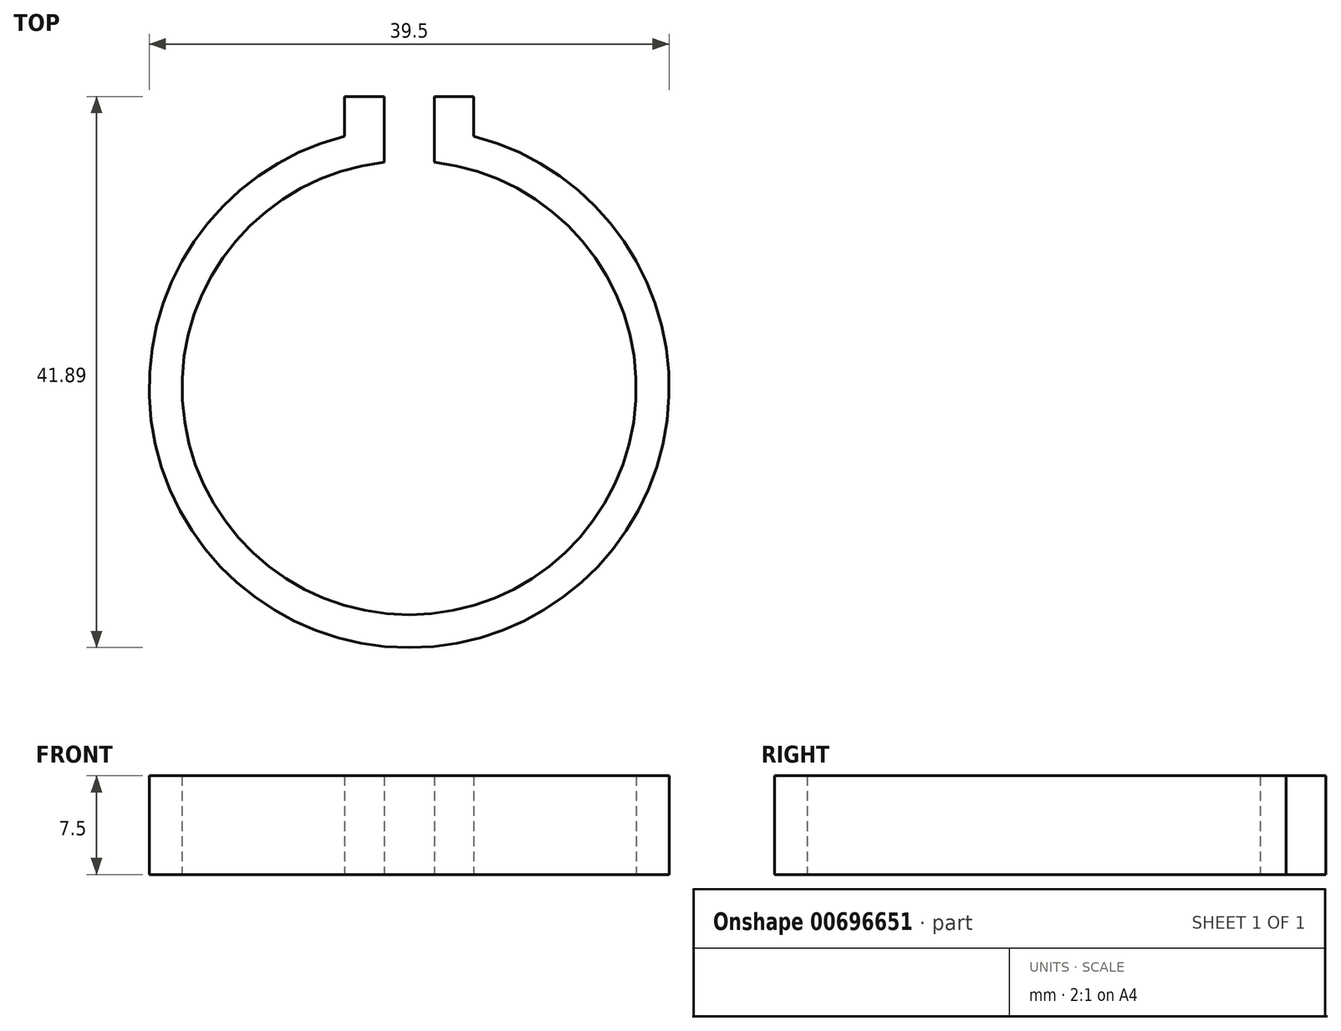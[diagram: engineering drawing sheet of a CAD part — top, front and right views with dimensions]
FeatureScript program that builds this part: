
annotation { "Feature Type Name" : "Feature", "Feature Type Description" : "" }
export const myFeature = defineFeature(function(context is Context, id is Id, definition is map)
    precondition{}
    {
        {
            var Q0;
            Q0=qCreatedBy(makeId("Top.planeOp"),FACE);
            var sketch = newSketch(context, id + "F0", { "sketchPlane" : qUnion([Q0])});
            skArc(sketch, "E0", {"start": v(-1.9, 17.14) * mm, "mid": v(0, -17.25) * mm, "end": v(1.9, 17.14) * mm});
            skArc(sketch, "E1.0", {"start": v(-4.9, 19.13) * mm, "mid": v(0, -19.75) * mm, "end": v(4.9, 19.13) * mm});
            skLineSegment(sketch, "E2.left", {"start": v(1.9, 19.66) * mm, "end": v(1.9, 17.14) * mm});
            skLineSegment(sketch, "E2.right", {"start": v(-1.9, 19.66) * mm, "end": v(-1.9, 17.14) * mm});
            skPoint(sketch, "E2.middle", {"position": v(0, 17.25) * mm});
            skPoint(sketch, "E3.orphan", {"position": v(1.9, 14.84) * mm});
            skPoint(sketch, "E4.orphan", {"position": v(-1.9, 14.84) * mm});
            skLineSegment(sketch, "E5.top", {"start": v(-1.9, 22.14) * mm, "end": v(-4.9, 22.14) * mm});
            skLineSegment(sketch, "E5.left", {"start": v(-1.9, 17.14) * mm, "end": v(-1.9, 22.14) * mm});
            skLineSegment(sketch, "E5.right", {"start": v(-4.9, 19.13) * mm, "end": v(-4.9, 22.14) * mm});
            skLineSegment(sketch, "E6.top", {"start": v(1.9, 22.14) * mm, "end": v(4.9, 22.14) * mm});
            skLineSegment(sketch, "E6.left", {"start": v(1.9, 17.14) * mm, "end": v(1.9, 22.14) * mm});
            skLineSegment(sketch, "E6.right", {"start": v(4.9, 19.13) * mm, "end": v(4.9, 22.14) * mm});
            skSolve(sketch);
        }
        {
            var Q0;
            Q0 = qSketchRegion(id + "F0", true);
            extrude(context, id + "F1", {"entities" : qUnion([Q0]), "depth" : 7.5 * mm, "offsetDistance" : 25.4 * mm});
        }
    });
